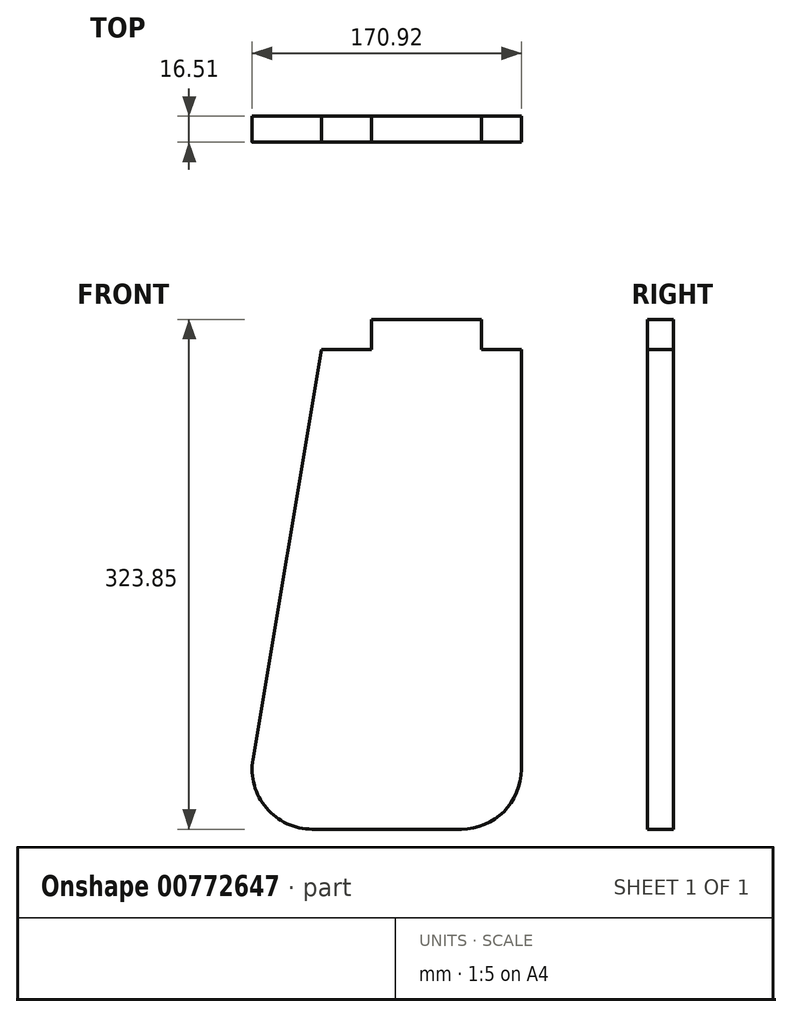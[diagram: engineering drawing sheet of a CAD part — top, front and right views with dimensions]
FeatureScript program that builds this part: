
annotation { "Feature Type Name" : "Feature", "Feature Type Description" : "" }
export const myFeature = defineFeature(function(context is Context, id is Id, definition is map)
    precondition{}
    {
        {
            var Q0;
            Q0=qCreatedBy(makeId("Front.planeOp"),FACE);
            var sketch = newSketch(context, id + "F0", { "sketchPlane" : qUnion([Q0])});
            skLineSegment(sketch, "E0", {"start": v(-0.06, -140.84) * mm, "end": v(-0.06, -445.64) * mm});
            skLineSegment(sketch, "E1", {"start": v(-0.06, -140.84) * mm, "end": v(-25.46, -140.84) * mm});
            skLineSegment(sketch, "E2", {"start": v(-25.46, -140.84) * mm, "end": v(-25.46, -121.79) * mm});
            skLineSegment(sketch, "E3", {"start": v(-25.46, -121.79) * mm, "end": v(-95.3, -121.79) * mm});
            skLineSegment(sketch, "E4", {"start": v(-95.3, -121.79) * mm, "end": v(-95.3, -140.84) * mm});
            skLineSegment(sketch, "E5", {"start": v(-0.06, -445.64) * mm, "end": v(-177.86, -445.64) * mm});
            skLineSegment(sketch, "E6", {"start": v(-95.3, -140.84) * mm, "end": v(-127.06, -140.83) * mm});
            skLineSegment(sketch, "E7", {"start": v(-127.06, -140.83) * mm, "end": v(-177.86, -445.64) * mm});
            skSolve(sketch);
        }
        {
            var Q0;
            Q0 = qSketchRegion(id + "F0", true);
            extrude(context, id + "F1", {"entities" : qUnion([Q0]), "depth" : 16.5 * mm, "offsetDistance" : 25.4 * mm});
        }
        {
            var Q0;
            Q0=makeQuery(id+"F1.opExtrude","SWEPT_EDGE",EDGE,{"disambiguationData":[OSD([sQuery(id+"F0.wireOp",EDGE,"E5"),sQuery(id+"F0.wireOp",EDGE,"E7")])]});
            fillet(context, id + "F2", {"entities" : qUnion([Q0]), "radius" : 38.1 * mm, "tangentPropagation" : true, "allowEdgeOverflow" : false});
        }
        {
            var Q0;
            Q0=makeQuery(id+"F1.opExtrude","SWEPT_EDGE",EDGE,{"disambiguationData":[OSD([sQuery(id+"F0.wireOp",EDGE,"E0"),sQuery(id+"F0.wireOp",EDGE,"E5")])]});
            fillet(context, id + "F3", {"entities" : qUnion([Q0]), "radius" : 38.1 * mm, "tangentPropagation" : true, "allowEdgeOverflow" : false});
        }
    });
